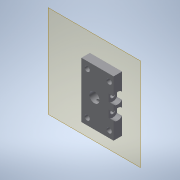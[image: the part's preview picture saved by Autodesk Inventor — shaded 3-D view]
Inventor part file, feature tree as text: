
AUTODESK INVENTOR PART (.ipt)
format: ipt  version: 2022 (Build 260153000, 153)  size: 173,056 bytes
history: native  units: mm
features: reference x7, other x5, projected_geometry x3, sketch x2, plane x1, extrude x1, hole x1
ambient origin geometry x8: Origin, YZ Plane, XZ Plane, XY Plane, X Axis, Y Axis, Z Axis, Center Point
bodies: Volumenkörper1 (feature_tree)
feature tree (20):
  plane  "Arbeitsebene1"
  extrude  "Extrusion1"  Depth=0.5mm
  hole  "Bohrung2"  [1 undecoded]
  sketch  "Skizze1"  dims[d0=0.5mm d1=0.5mm]
  reference  "Referenz1"
  reference  "Referenz2"
  reference  "Referenz3"
  reference  "Referenz4"
  reference  "Referenz5"
  reference  "Referenz6"
  reference  "Referenz13"
  sketch  "Skizze5"  dims[d2=5.0mm d3=0.0mm d19=2.8mm d20=2.8mm d25=6.0mm d26=2.8mm d27=6.0mm d28=6.5mm d29=3.0mm d30=90.0deg d31=30.0mm d32=0.0mm]
  projected_geometry  "Projizierte Kontur1"
  projected_geometry  "Projizierte Kontur2"
  projected_geometry  "Projizierte Kontur3"
  other  "Assembly_Cube_Z-Stage_NEMA8_captive_v0.iam"
  other  "30_Cube_Z_Focus_NEMA8_captive_base_v0:1"
  other  "Assembly_Cube_empty_IM_v3:3"
  other  "10_Cube_1x1_IM:1"
  other  "00_RS_Pro_Micrometer_small:1"
note: 1 required parameter value undecoded (feature->parameter linkage not recoverable at this tier; creation-order binding heuristic only, values carry confidence <= 0.55)
